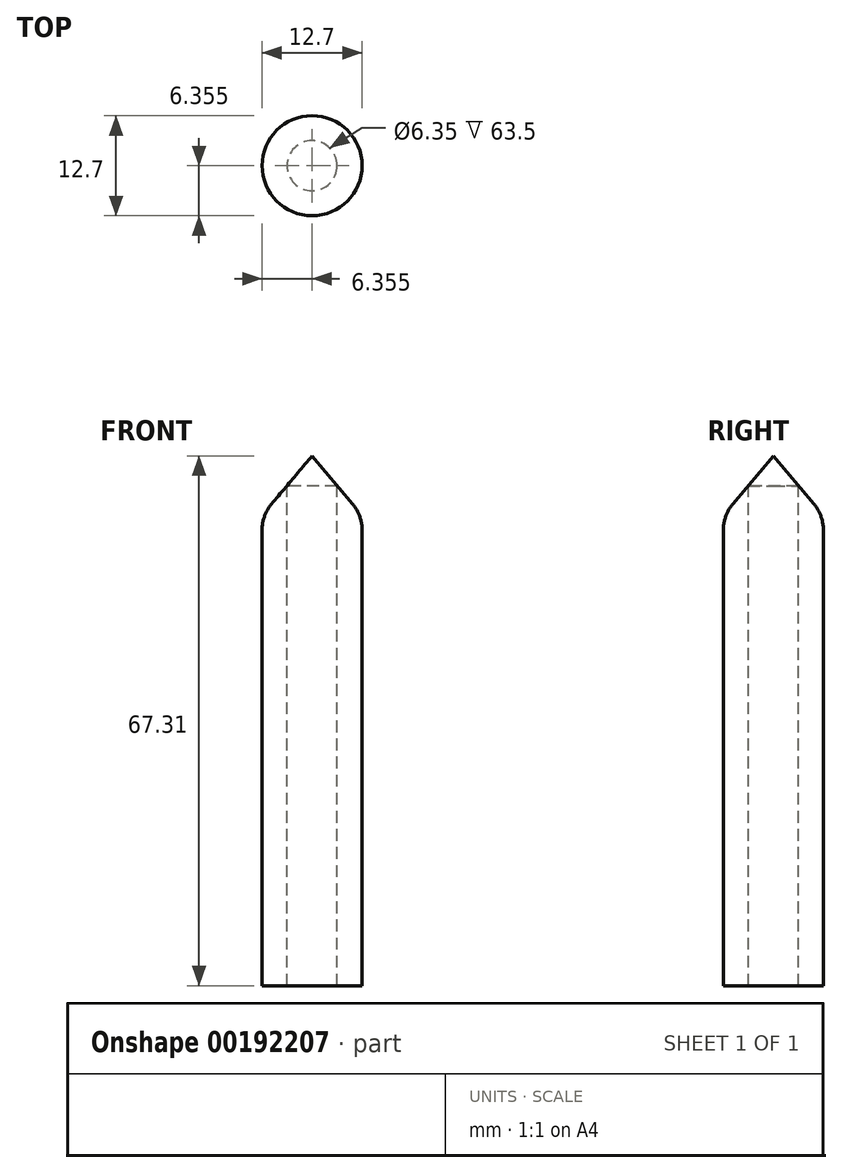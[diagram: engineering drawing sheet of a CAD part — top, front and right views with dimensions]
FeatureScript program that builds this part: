
annotation { "Feature Type Name" : "Feature", "Feature Type Description" : "" }
export const myFeature = defineFeature(function(context is Context, id is Id, definition is map)
    precondition{}
    {
        {
            var Q0;
            Q0=qCreatedBy(makeId("Top.planeOp"),FACE);
            var sketch = newSketch(context, id + "F0", { "sketchPlane" : qUnion([Q0])});
            skCircle(sketch, "E0", {"center": v(-23.02, -49.18) * mm, "radius": 6.35 * mm});
            skSolve(sketch);
        }
        {
            var Q0;
            Q0=makeQuery(id+"F0.imprint","IMPRINT",FACE,{"disambiguationData":[TD([[makeQuery(id+"F0.imprint","IMPRINT",EDGE,{"derivedFrom":sQuery(id+"F0.wireOp",EDGE,"E0")}),1.0]])]});
            extrude(context, id + "F1", {"entities" : qUnion([Q0]), "depth" : 63.5 * mm});
        }
        {
            var Q0;
            Q0=makeQuery(id+"F1.opExtrude","CAP_FACE",FACE,{"disambiguationData":[OSD([sQuery(id+"F0.wireOp",EDGE,"E0")])],"isStart":false});
            var sketch = newSketch(context, id + "F2", { "sketchPlane" : qUnion([Q0])});
            skCircle(sketch, "E1", {"center": v(-23.02, -49.18) * mm, "radius": 6.35 * mm});
            skSolve(sketch);
        }
        {
            var Q0;
            Q0=makeQuery(id+"F1.opExtrude","CAP_FACE",FACE,{"disambiguationData":[OSD([sQuery(id+"F0.wireOp",EDGE,"E0")])],"isStart":false});
            var sketch = newSketch(context, id + "F3", { "sketchPlane" : qUnion([Q0])});
            skSolve(sketch);
        }
        {
            var Q0;
            Q0=qSketchRegion(id+"F3",true);
            var Q1;
            Q1=makeQuery(id+"F3.imprint","IMPRINT",FACE,{"disambiguationData":[TD([[makeQuery(id+"F3.imprint","IMPRINT",EDGE,{"derivedFrom":makeQuery(id+"F1.opExtrude","CAP_EDGE",EDGE,{"disambiguationData":[OSD([sQuery(id+"F0.wireOp",EDGE,"E0")])],"isStart":false})}),1.0]])]});
            extrude(context, id + "F4", {"entities" : qUnion([Q0, Q1]), "operationType" : NewBodyOperationType.ADD, "depth" : 3.8 * mm});
        }
        {
            var Q0;
            Q0=sQuery(id+"F2.wireOp",VERTEX,"E1.center");
            var Q1;
            Q1=makeQuery(id+"F1.opExtrude","SWEPT_BODY",BODY,{"disambiguationData":[OSD([sQuery(id+"F0.wireOp",EDGE,"E0")])]});
            hole(context, id + "F5", {"style" : HoleStyle.SIMPLE, "endStyle" : HoleEndStyle.BLIND, "holeDiameter" : 6.35 * mm, "holeDepth" : 63.5 * mm, "startFromSketch" : true, "locations" : qUnion([Q0]), "scope" : qUnion([Q1])});
        }
        {
            var Q0;
            Q0=makeQuery(id+"F4.opExtrude","CAP_EDGE",EDGE,{"disambiguationData":[OSD([sQuery(id+"F0.wireOp",EDGE,"E0")])],"isStart":false});
            chamfer(context, id + "F6", {"entities" : qUnion([Q0]), "chamferType" : ChamferType.OFFSET_ANGLE, "width" : 6.35 * mm, "oppositeDirection" : false, "angle" : 50 * degree, "tangentPropagation" : true});
        }
        {
            var Q0;
            {var subQ0=sQuery(id+"F0.wireOp",EDGE,"E0");Q0=makeQuery(id+"F6.opChamfer","BLEND_EDGE",EDGE,{"blendedFrom":[makeQuery(id+"F4.opExtrude","CAP_EDGE",EDGE,{"disambiguationData":[OSD([subQ0])],"isStart":false}),makeQuery(id+"F4.boolean.opBoolean","MERGE",FACE,{"derivedFrom":[makeQuery(id+"F1.opExtrude","SWEPT_FACE",FACE,{"disambiguationData":[OSD([subQ0])]}),makeQuery(id+"F4.opExtrude","SWEPT_FACE",FACE,{"disambiguationData":[OSD([subQ0])]})]})],"blendedInto":[makeQuery(id+"F4.boolean.opBoolean","MERGE",FACE,{"derivedFrom":[makeQuery(id+"F1.opExtrude","SWEPT_FACE",FACE,{"disambiguationData":[OSD([subQ0])]}),makeQuery(id+"F4.opExtrude","SWEPT_FACE",FACE,{"disambiguationData":[OSD([subQ0])]})]})]});}
            fillet(context, id + "F7", {"entities" : qUnion([Q0]), "radius" : 5.08 * mm, "tangentPropagation" : true, "allowEdgeOverflow" : false});
        }
    });
